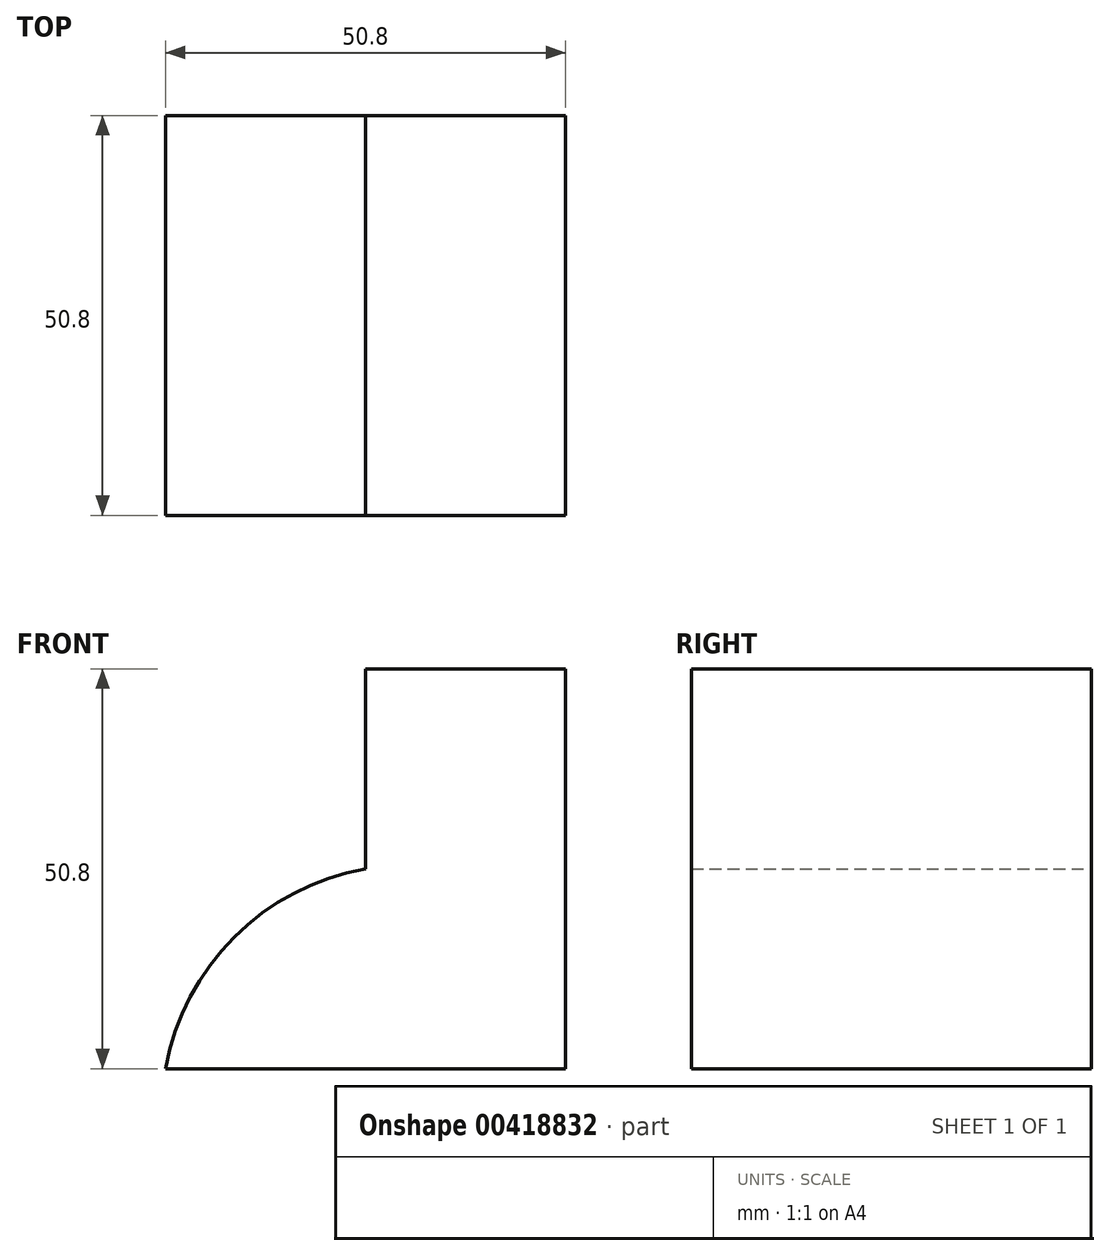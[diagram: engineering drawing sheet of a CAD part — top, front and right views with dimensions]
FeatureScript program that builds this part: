
annotation { "Feature Type Name" : "Feature", "Feature Type Description" : "" }
export const myFeature = defineFeature(function(context is Context, id is Id, definition is map)
    precondition{}
    {
        {
            var Q0;
            Q0=qCreatedBy(makeId("Front.planeOp"),FACE);
            var sketch = newSketch(context, id + "F0", { "sketchPlane" : qUnion([Q0])});
            skLineSegment(sketch, "E0", {"start": v(0, 0) * mm, "end": v(-50.8, 0) * mm});
            skLineSegment(sketch, "E1", {"start": v(0, 0) * mm, "end": v(0, 50.8) * mm});
            skLineSegment(sketch, "E2", {"start": v(0, 50.8) * mm, "end": v(-25.4, 50.8) * mm});
            skLineSegment(sketch, "E3", {"start": v(-25.4, 50.8) * mm, "end": v(-25.4, 25.4) * mm});
            skArc(sketch, "E4", {"start": v(-25.4, 25.4) * mm, "mid": v(-42.09, 16.69) * mm, "end": v(-50.8, 0) * mm});
            skSolve(sketch);
        }
        {
            var Q0;
            Q0=makeQuery(id+"F0.imprint","IMPRINT",FACE,{"disambiguationData":[TD([[makeQuery(id+"F0.imprint","IMPRINT",EDGE,{"derivedFrom":sQuery(id+"F0.wireOp",EDGE,"E0")}),-1.0]])]});
            extrude(context, id + "F1", {"entities" : qUnion([Q0]), "depth" : 50.8 * mm});
        }
    });
